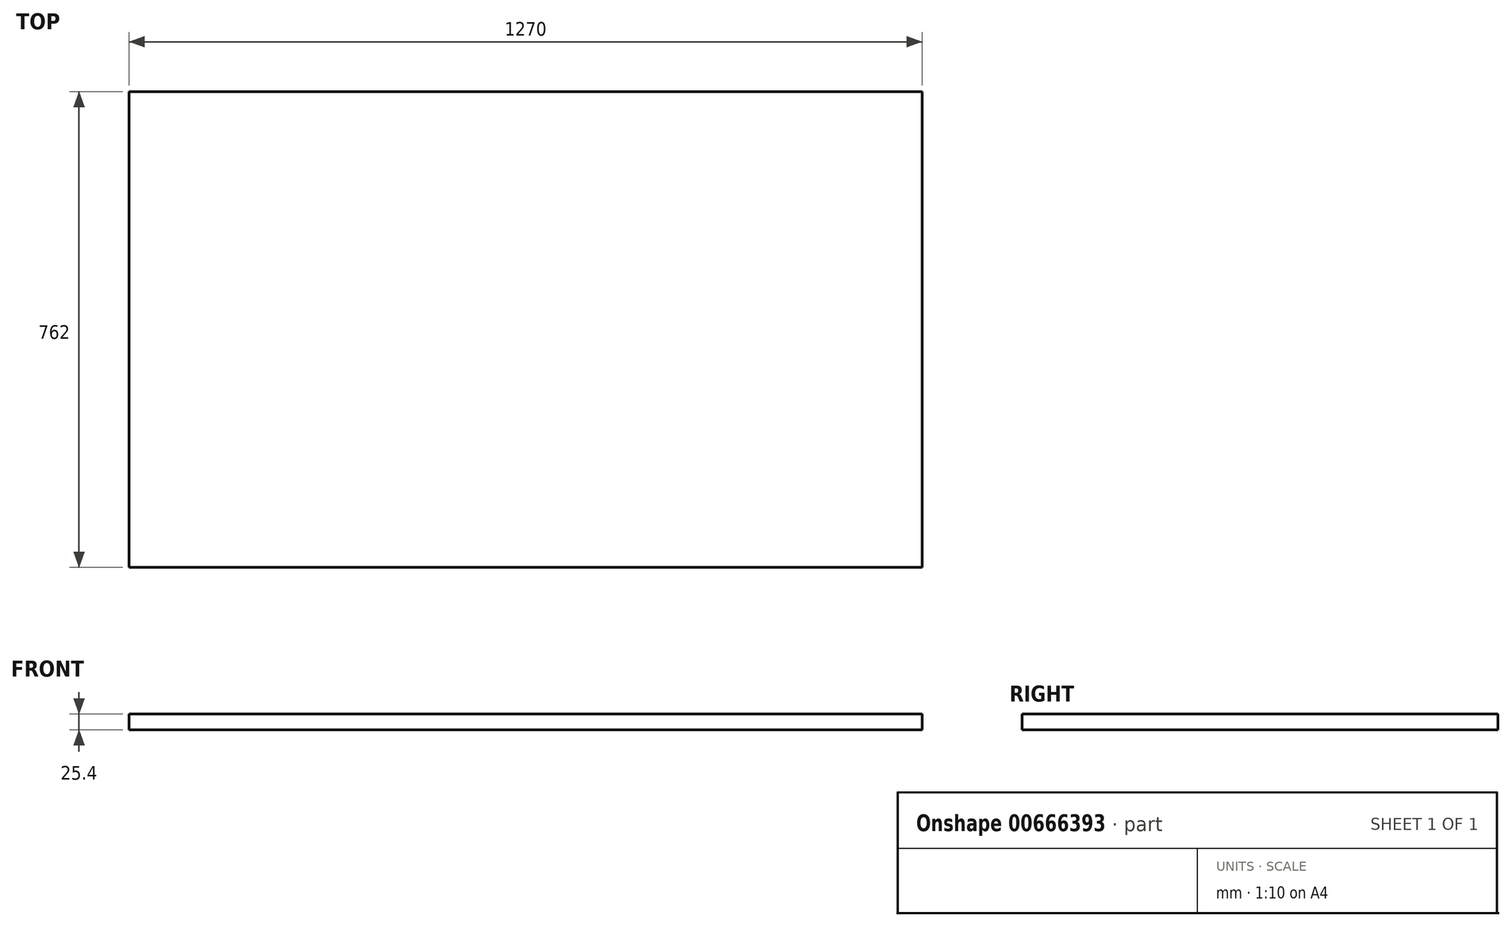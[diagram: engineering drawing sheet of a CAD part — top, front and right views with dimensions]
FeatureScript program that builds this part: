
annotation { "Feature Type Name" : "Feature", "Feature Type Description" : "" }
export const myFeature = defineFeature(function(context is Context, id is Id, definition is map)
    precondition{}
    {
        {
            var Q0;
            Q0=qCreatedBy(makeId("Top.planeOp"),FACE);
            var sketch = newSketch(context, id + "F0", { "sketchPlane" : qUnion([Q0])});
            skLineSegment(sketch, "E0.bottom", {"start": v(0, 0) * mm, "end": v(1270, 0) * mm});
            skLineSegment(sketch, "E0.top", {"start": v(0, 762) * mm, "end": v(1270, 762) * mm});
            skLineSegment(sketch, "E0.left", {"start": v(0, 0) * mm, "end": v(0, 762) * mm});
            skLineSegment(sketch, "E0.right", {"start": v(1270, 0) * mm, "end": v(1270, 762) * mm});
            skSolve(sketch);
        }
        {
            var Q0;
            Q0 = qSketchRegion(id + "F0", true);
            extrude(context, id + "F1", {"entities" : qUnion([Q0]), "depth" : 25.4 * mm, "offsetDistance" : 25.4 * mm});
        }
    });
